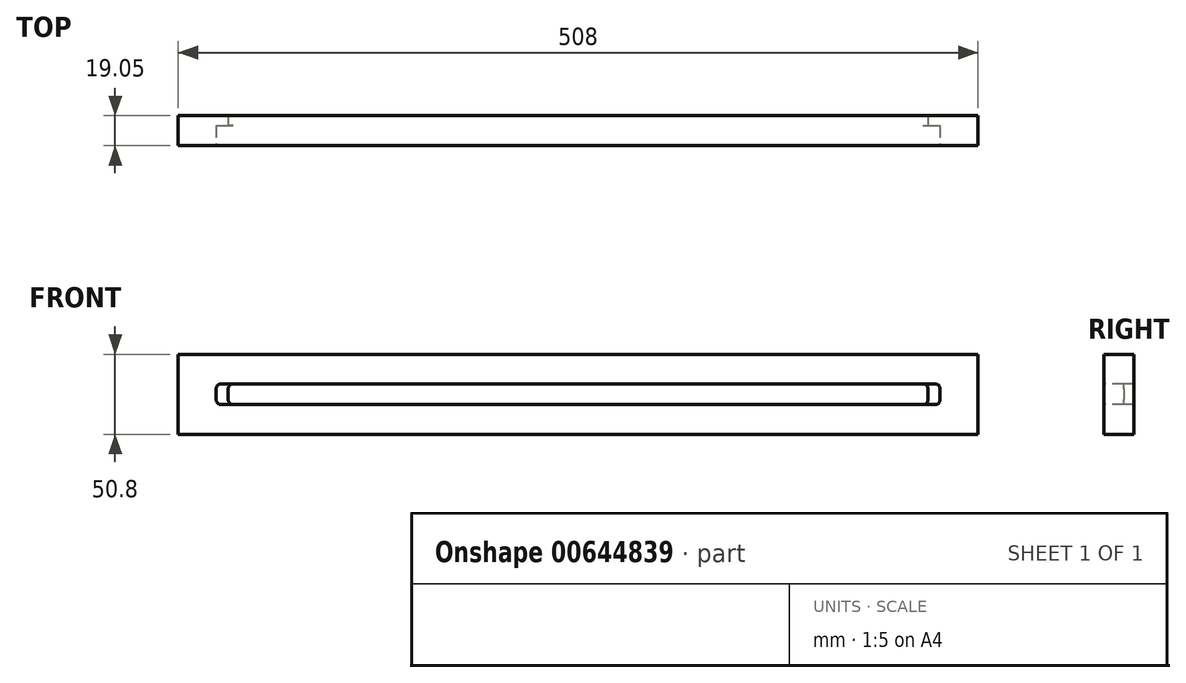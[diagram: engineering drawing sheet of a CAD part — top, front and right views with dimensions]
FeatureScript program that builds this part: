
annotation { "Feature Type Name" : "Feature", "Feature Type Description" : "" }
export const myFeature = defineFeature(function(context is Context, id is Id, definition is map)
    precondition{}
    {
        {
            var Q0;
            Q0=qCreatedBy(makeId("Front.planeOp"),FACE);
            var sketch = newSketch(context, id + "F0", { "sketchPlane" : qUnion([Q0])});
            skLineSegment(sketch, "E0.bottom", {"start": v(0, 0) * mm, "end": v(508, 0) * mm});
            skLineSegment(sketch, "E0.top", {"start": v(0, 50.8) * mm, "end": v(508, 50.8) * mm});
            skLineSegment(sketch, "E0.left", {"start": v(0, 0) * mm, "end": v(0, 50.8) * mm});
            skLineSegment(sketch, "E0.right", {"start": v(508, 0) * mm, "end": v(508, 50.8) * mm});
            skSolve(sketch);
        }
        {
            var Q0;
            Q0=makeQuery(id+"F0.imprint","IMPRINT",FACE,{"disambiguationData":[TD([[makeQuery(id+"F0.imprint","IMPRINT",EDGE,{"derivedFrom":sQuery(id+"F0.wireOp",EDGE,"E0.bottom")}),1.0]])]});
            extrude(context, id + "F1", {"entities" : qUnion([Q0]), "depth" : 19.05 * mm, "offsetDistance" : 25.4 * mm});
        }
        {
            var Q0;
            Q0=makeQuery(id+"F1.opExtrude","CAP_FACE",FACE,{"disambiguationData":[OSD([sQuery(id+"F0.wireOp",EDGE,"E0.bottom"),sQuery(id+"F0.wireOp",EDGE,"E0.top"),sQuery(id+"F0.wireOp",EDGE,"E0.left"),sQuery(id+"F0.wireOp",EDGE,"E0.right")])],"isStart":false});
            var sketch = newSketch(context, id + "F2", { "sketchPlane" : qUnion([Q0])});
            skLineSegment(sketch, "E1.bottom", {"start": v(27.3, 32) * mm, "end": v(480.7, 32) * mm});
            skLineSegment(sketch, "E1.top", {"start": v(27.3, 18.8) * mm, "end": v(480.7, 18.8) * mm});
            skLineSegment(sketch, "E1.left", {"start": v(24.13, 28.83) * mm, "end": v(24.13, 21.97) * mm});
            skLineSegment(sketch, "E1.right", {"start": v(483.87, 28.83) * mm, "end": v(483.87, 21.97) * mm});
            skPoint(sketch, "E2.visualSharp", {"position": v(24.13, 32) * mm});
            skArc(sketch, "E2.filletArc", {"start": v(27.3, 32) * mm, "mid": v(25.06, 31.07) * mm, "end": v(24.13, 28.83) * mm});
            skPoint(sketch, "E3.visualSharp", {"position": v(24.13, 18.8) * mm});
            skArc(sketch, "E3.filletArc", {"start": v(24.13, 21.97) * mm, "mid": v(25.06, 19.73) * mm, "end": v(27.3, 18.8) * mm});
            skPoint(sketch, "E4.visualSharp", {"position": v(483.87, 18.8) * mm});
            skArc(sketch, "E4.filletArc", {"start": v(480.7, 18.8) * mm, "mid": v(482.94, 19.73) * mm, "end": v(483.87, 21.97) * mm});
            skPoint(sketch, "E5.visualSharp", {"position": v(483.87, 32) * mm});
            skArc(sketch, "E5.filletArc", {"start": v(483.87, 28.83) * mm, "mid": v(482.94, 31.07) * mm, "end": v(480.7, 32) * mm});
            skSolve(sketch);
        }
        {
            var Q0;
            Q0=makeQuery(id+"F2.imprint","IMPRINT",FACE,{"disambiguationData":[TD([[makeQuery(id+"F2.imprint","IMPRINT",EDGE,{"derivedFrom":sQuery(id+"F2.wireOp",EDGE,"E1.bottom")}),-1.0]])]});
            extrude(context, id + "F3", {"entities" : qUnion([Q0]), "operationType" : NewBodyOperationType.REMOVE, "oppositeDirection" : true, "depth" : 12.7 * mm, "offsetDistance" : 25.4 * mm});
        }
        {
            var Q0;
            Q0=makeQuery(id+"F1.opExtrude","CAP_FACE",FACE,{"disambiguationData":[OSD([sQuery(id+"F0.wireOp",EDGE,"E0.bottom"),sQuery(id+"F0.wireOp",EDGE,"E0.top"),sQuery(id+"F0.wireOp",EDGE,"E0.left"),sQuery(id+"F0.wireOp",EDGE,"E0.right")])],"isStart":false});
            var sketch = newSketch(context, id + "F4", { "sketchPlane" : qUnion([Q0])});
            skLineSegment(sketch, "E6.bottom", {"start": v(34.93, 32) * mm, "end": v(473.08, 32) * mm});
            skLineSegment(sketch, "E6.top", {"start": v(34.93, 18.8) * mm, "end": v(473.08, 18.8) * mm});
            skLineSegment(sketch, "E6.left", {"start": v(31.75, 28.83) * mm, "end": v(31.75, 21.97) * mm});
            skLineSegment(sketch, "E6.right", {"start": v(476.25, 28.83) * mm, "end": v(476.25, 21.97) * mm});
            skPoint(sketch, "E7.visualSharp", {"position": v(476.25, 18.8) * mm});
            skArc(sketch, "E7.filletArc", {"start": v(473.08, 18.8) * mm, "mid": v(475.32, 19.73) * mm, "end": v(476.25, 21.97) * mm});
            skPoint(sketch, "E8.visualSharp", {"position": v(476.25, 32) * mm});
            skArc(sketch, "E8.filletArc", {"start": v(476.25, 28.83) * mm, "mid": v(475.32, 31.07) * mm, "end": v(473.08, 32) * mm});
            skPoint(sketch, "E9.visualSharp", {"position": v(31.75, 18.8) * mm});
            skArc(sketch, "E9.filletArc", {"start": v(31.75, 21.97) * mm, "mid": v(32.68, 19.73) * mm, "end": v(34.93, 18.8) * mm});
            skPoint(sketch, "E10.visualSharp", {"position": v(31.75, 32) * mm});
            skArc(sketch, "E10.filletArc", {"start": v(34.93, 32) * mm, "mid": v(32.68, 31.07) * mm, "end": v(31.75, 28.83) * mm});
            skSolve(sketch);
        }
        {
            var Q0;
            Q0=makeQuery(id+"F4.imprint","IMPRINT",FACE,{"disambiguationData":[TD([[makeQuery(id+"F4.imprint","IMPRINT",EDGE,{"derivedFrom":sQuery(id+"F4.wireOp",EDGE,"E6.bottom")}),-1.0]])]});
            extrude(context, id + "F5", {"entities" : qUnion([Q0]), "operationType" : NewBodyOperationType.REMOVE, "oppositeDirection" : true, "depth" : 25.4 * mm, "offsetDistance" : 25.4 * mm});
        }
    });
